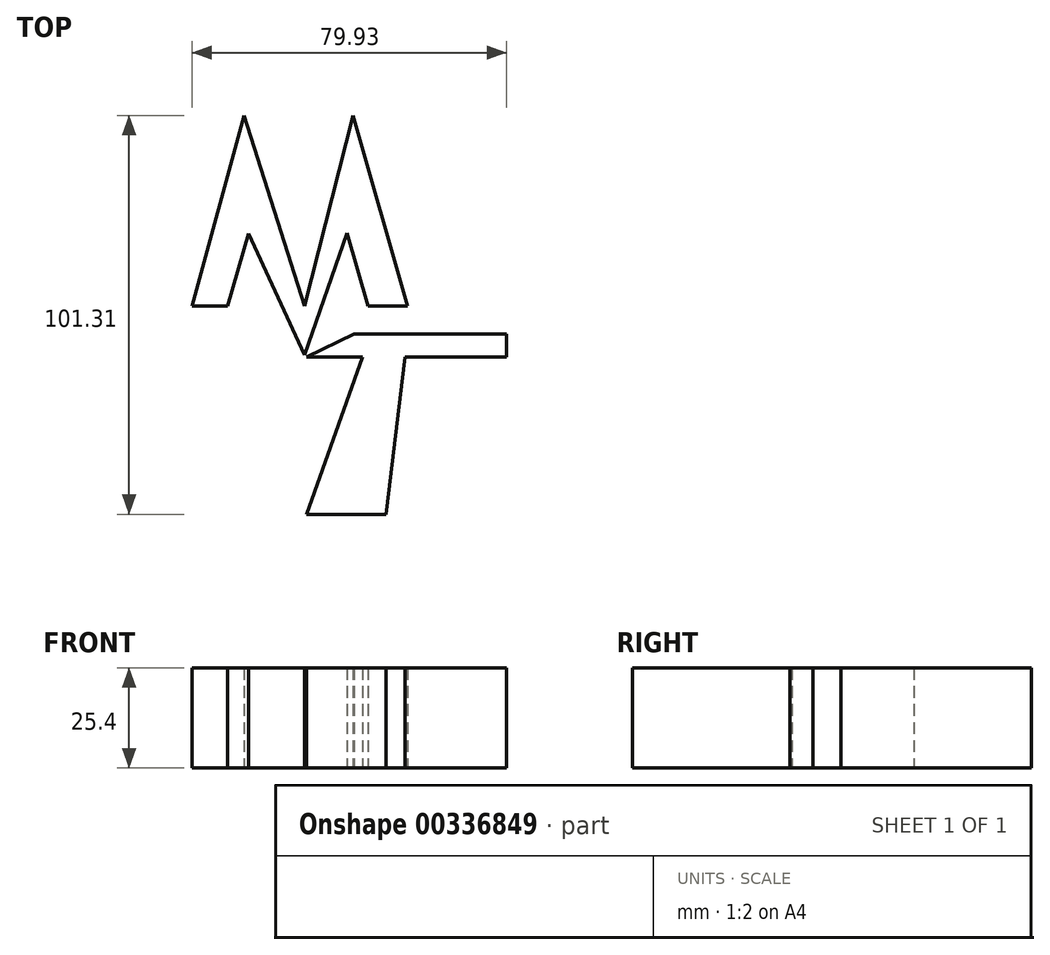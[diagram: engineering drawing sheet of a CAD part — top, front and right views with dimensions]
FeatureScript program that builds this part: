
annotation { "Feature Type Name" : "Feature", "Feature Type Description" : "" }
export const myFeature = defineFeature(function(context is Context, id is Id, definition is map)
    precondition{}
    {
        {
            var Q0;
            Q0=qCreatedBy(makeId("Top.planeOp"),FACE);
            var sketch = newSketch(context, id + "F0", { "sketchPlane" : qUnion([Q0])});
            skFitSpline(sketch, "E0", {"points": [v(0, 0) * mm, v(13.26, 48.42) * mm], "startDerivative": vector(13.26, 48.42) * mm, "endDerivative": vector(13.26, 48.42) * mm});
            skLineSegment(sketch, "E1", {"start": v(13.26, 48.42) * mm, "end": v(28.63, 0) * mm});
            skLineSegment(sketch, "E2", {"start": v(28.63, 0) * mm, "end": v(40.93, 48.42) * mm});
            skLineSegment(sketch, "E3", {"start": v(40.93, 48.42) * mm, "end": v(54.76, 0) * mm});
            skLineSegment(sketch, "E4", {"start": v(0, 0) * mm, "end": v(9, 0) * mm});
            skLineSegment(sketch, "E5", {"start": v(9, 0) * mm, "end": v(14.36, 18.53) * mm});
            skLineSegment(sketch, "E6", {"start": v(14.36, 18.53) * mm, "end": v(28.63, -12.4) * mm});
            skLineSegment(sketch, "E7", {"start": v(54.76, 0) * mm, "end": v(44.7, 0) * mm});
            skLineSegment(sketch, "E8", {"start": v(44.7, 0) * mm, "end": v(39.4, 18.58) * mm});
            skLineSegment(sketch, "E9", {"start": v(39.4, 18.58) * mm, "end": v(28.63, -12.4) * mm});
            skSolve(sketch);
        }
        {
            var Q0;
            Q0 = qSketchRegion(id + "F0", true);
            extrude(context, id + "F1", {"entities" : qUnion([Q0]), "depth" : 25.4 * mm});
        }
        {
            var Q0;
            Q0=qCreatedBy(makeId("Top.planeOp"),FACE);
            var sketch = newSketch(context, id + "F2", { "sketchPlane" : qUnion([Q0])});
            skLineSegment(sketch, "E10", {"start": v(29.13, -12.89) * mm, "end": v(79.93, -12.89) * mm});
            skLineSegment(sketch, "E11", {"start": v(79.93, -7.02) * mm, "end": v(79.93, -12.89) * mm});
            skLineSegment(sketch, "E12", {"start": v(79.93, -7.02) * mm, "end": v(41.12, -7.02) * mm});
            skLineSegment(sketch, "E13", {"start": v(29.13, -12.89) * mm, "end": v(41.12, -7.02) * mm});
            skLineSegment(sketch, "E14", {"start": v(45.36, -7.02) * mm, "end": v(29.13, -52.9) * mm});
            skLineSegment(sketch, "E15", {"start": v(29.13, -52.9) * mm, "end": v(49.27, -52.9) * mm});
            skLineSegment(sketch, "E16", {"start": v(49.27, -52.9) * mm, "end": v(54.82, -7.02) * mm});
            skSolve(sketch);
        }
        {
            var Q0;
            Q0 = qSketchRegion(id + "F2", true);
            extrude(context, id + "F3", {"entities" : qUnion([Q0]), "depth" : 25.4 * mm});
        }
    });
